MODEL slx_e30d3c3d6ad5
CONFIG AbsTol = auto
CONFIG FixedStep = 0.001
CONFIG MaxStep = auto
CONFIG MinStep = auto
CONFIG RelTol = 1e-3
CONFIG SampleTimeConstraint = Unconstrained
CONFIG Solver = ode4
CONFIG SolverMode = Auto
CONFIG SolverName = ode4
CONFIG StartTime = 0.0
CONFIG StopTime = 15
BLOCK [SubSystem] Control Law Block
  Ports = [2, 1]
  RequestExecContextInheritance = off
BLOCK [Constant] Control Law Block/Constant
  Value = d
BLOCK [SubSystem] Control Law Block/MATLAB Function
  ErrorFcn = Stateflow.Translate.translate
  PermitHierarchicalResolution = ExplicitOnly
  Ports = [2, 1]
  RequestExecContextInheritance = off
  SFBlockType = MATLAB Function
  TreatAsAtomicUnit = on
BLOCK [Demux] Control Law Block/MATLAB Function/ Demux 
  Outputs = 1
  Ports = [1, 1]
BLOCK [S-Function] Control Law Block/MATLAB Function/ SFunction 
  EnableBusSupport = on
  FunctionName = sf_sfun
  PortCounts = [2 2]
  Ports = [2, 2]
  Tag = Stateflow S-Function StaticControl 2
BLOCK [Terminator] Control Law Block/MATLAB Function/ Terminator 
BLOCK [Outport] Control Law Block/MATLAB Function/K_inv
  IconDisplay = Port number
BLOCK [Inport] Control Law Block/MATLAB Function/d
  IconDisplay = Port number
BLOCK [Inport] Control Law Block/MATLAB Function/theta
  IconDisplay = Port number
  Port = 2
BLOCK [Product] Control Law Block/Product
  InputSameDT = off
  Multiplication = Matrix(*)
  OutDataTypeStr = Inherit: Inherit via internal rule
  Ports = [2, 1]
  RndMeth = Floor
  SaturateOnIntegerOverflow = off
BLOCK [Inport] Control Law Block/W
  IconDisplay = Port number
BLOCK [Inport] Control Law Block/theta
  IconDisplay = Port number
  Port = 2
BLOCK [Outport] Control Law Block/u_m
  IconDisplay = Port number
BLOCK [SubSystem] DKM
  Ports = [1, 3]
  RequestExecContextInheritance = off
BLOCK [Demux] DKM/Demux
  DisplayOption = bar
  Outputs = 2
  Ports = [1, 2]
BLOCK [Constant] DKM/F_inv
  Value = [r/2 r/2; r/(2*L) -r/(2*L)]
BLOCK [Fcn] DKM/Fcn
  Expr = cos(u)
BLOCK [Fcn] DKM/Fcn1
  Expr = sin(u)
BLOCK [Integrator] DKM/Integrator
  InitialCondition = theta0
  Ports = [1, 1]
BLOCK [Product] DKM/Product
  InputSameDT = off
  OutDataTypeStr = Inherit: Inherit via internal rule
  Ports = [2, 1]
  RndMeth = Floor
  SaturateOnIntegerOverflow = off
BLOCK [Product] DKM/Product1
  InputSameDT = off
  OutDataTypeStr = Inherit: Inherit via internal rule
  Ports = [2, 1]
  RndMeth = Floor
  SaturateOnIntegerOverflow = off
BLOCK [Scope] DKM/Scope
  Floating = off
  NumInputPorts = 1
  Ports = [1]
BLOCK [ToWorkspace] DKM/To Workspace
  FixptAsFi = on
  MaxDataPoints = inf
  Ports = [1]
  SampleTime = -1
  Save2DSignal = 3-D array (concatenate along third dimension)
  VariableName = u
BLOCK [Inport] DKM/qm_dot
  IconDisplay = Port number
BLOCK [Outport] DKM/theta
  IconDisplay = Port number
  Port = 3
BLOCK [Product] DKM/u_m Func
  InputSameDT = off
  Multiplication = Matrix(*)
  OutDataTypeStr = Inherit: Inherit via internal rule
  Ports = [2, 1]
  RndMeth = Floor
  SaturateOnIntegerOverflow = off
BLOCK [Outport] DKM/x_dot
  IconDisplay = Port number
BLOCK [Outport] DKM/y_dot
  IconDisplay = Port number
  Port = 2
BLOCK [Gain] Gain
  Gain = K
  OutDataTypeStr = Inherit: Inherit via internal rule
  ParamDataTypeStr = Inherit: Inherit via internal rule
  SaturateOnIntegerOverflow = off
BLOCK [Gain] IKM
  Gain = [1/r_e L_e/r_e; 1/r_e  -L_e/r_e]
  Multiplication = Matrix(K*u) (u vector)
  OutDataTypeStr = Inherit: Inherit via internal rule
  ParamDataTypeStr = Inherit: Inherit via internal rule
  SaturateOnIntegerOverflow = off
BLOCK [SubSystem] Localization
  Ports = [3, 3]
  RequestExecContextInheritance = off
BLOCK [Integrator] Localization/Integrator1
  InitialCondition = x0
  Ports = [1, 1]
BLOCK [Integrator] Localization/Integrator2
  InitialCondition = y0
  Ports = [1, 1]
BLOCK [Mux] Localization/Mux
  DisplayOption = bar
  Inputs = 2
  Ports = [2, 1]
BLOCK [Mux] Localization/Mux1
  DisplayOption = bar
  Inputs = 2
  Ports = [2, 1]
BLOCK [Fcn] Localization/hx Func
  Expr = u(1)+d*cos(u(2))
BLOCK [Fcn] Localization/hy Func
  Expr = u(1)+d*sin(u(2))
BLOCK [Outport] Localization/theta
  IconDisplay = Port number
  Port = 3
BLOCK [Inport] Localization/theta 
  IconDisplay = Port number
  Port = 3
BLOCK [Outport] Localization/x
  IconDisplay = Port number
BLOCK [Inport] Localization/x_dot
  IconDisplay = Port number
BLOCK [Outport] Localization/y
  IconDisplay = Port number
  Port = 2
BLOCK [Inport] Localization/y_dot
  IconDisplay = Port number
  Port = 2
BLOCK [Mux] Mux
  DisplayOption = bar
  Inputs = 2
  Ports = [2, 1]
BLOCK [Mux] Mux1
  DisplayOption = bar
  Inputs = 2
  Ports = [2, 1]
BLOCK [Mux] Mux2
  DisplayOption = bar
  Inputs = 2
  Ports = [2, 1]
BLOCK [Mux] Mux3
  DisplayOption = bar
  Inputs = 3
  Ports = [3, 1]
BLOCK [Sum] Sum
  IconShape = round
  InputSameDT = off
  Inputs = -+|
  OutDataTypeStr = Inherit: Inherit via internal rule
  Ports = [2, 1]
  SaturateOnIntegerOverflow = off
BLOCK [Sum] Sum1
  IconShape = round
  InputSameDT = off
  Inputs = |++
  OutDataTypeStr = Inherit: Inherit via internal rule
  Ports = [2, 1]
  SaturateOnIntegerOverflow = off
BLOCK [ToWorkspace] To Workspace
  FixptAsFi = on
  MaxDataPoints = inf
  Ports = [1]
  SampleTime = -1
  Save2DSignal = 3-D array (concatenate along third dimension)
  VariableName = hd
BLOCK [ToWorkspace] To Workspace1
  FixptAsFi = on
  MaxDataPoints = inf
  Ports = [1]
  SampleTime = -1
  Save2DSignal = 3-D array (concatenate along third dimension)
  VariableName = h
BLOCK [ToWorkspace] To Workspace2
  FixptAsFi = on
  MaxDataPoints = inf
  Ports = [1]
  SampleTime = -1
  Save2DSignal = 3-D array (concatenate along third dimension)
  VariableName = error
BLOCK [SubSystem] Trajectory Generator
  Ports = [0, 4]
  RequestExecContextInheritance = off
BLOCK [SubSystem] Trajectory Generator/Circular Trajectory
  Ports = [0, 1]
  RequestExecContextInheritance = off
BLOCK [Constant] Trajectory Generator/Circular Trajectory/Constant
  Value = wd
BLOCK [Constant] Trajectory Generator/Circular Trajectory/Constant1
  Value = R
BLOCK [Fcn] Trajectory Generator/Circular Trajectory/Fcn
  Expr = u+pi/2
BLOCK [Integrator] Trajectory Generator/Circular Trajectory/Integrator
  Ports = [1, 1]
BLOCK [Mux] Trajectory Generator/Circular Trajectory/Mux
  DisplayOption = bar
  Inputs = 3
  Ports = [3, 1]
BLOCK [Mux] Trajectory Generator/Circular Trajectory/Mux1
  DisplayOption = bar
  Ports = [4, 1]
BLOCK [ToWorkspace] Trajectory Generator/Circular Trajectory/To Workspace
  FixptAsFi = on
  MaxDataPoints = inf
  Ports = [1]
  SampleTime = -1
  Save2DSignal = 3-D array (concatenate along third dimension)
  VariableName = thetad
BLOCK [Outport] Trajectory Generator/Circular Trajectory/[hd; hd_dot]
  IconDisplay = Port number
BLOCK [Fcn] Trajectory Generator/Circular Trajectory/xd Func
  Expr = u(3)*cos(u(2))
BLOCK [Fcn] Trajectory Generator/Circular Trajectory/xd_dot Func
  Expr = -u(3)*u(1)*sin(u(2))
BLOCK [Fcn] Trajectory Generator/Circular Trajectory/yd Func
  Expr = u(3)*sin(u(2))
BLOCK [Fcn] Trajectory Generator/Circular Trajectory/yd_dot Func
  Expr = u(3)*u(1)*cos(u(2))
BLOCK [Constant] Trajectory Generator/Constant
  Value = mode
BLOCK [Demux] Trajectory Generator/Demux
  DisplayOption = bar
  Ports = [1, 4]
BLOCK [SubSystem] Trajectory Generator/Fixed Point Tracking
  Ports = [0, 1]
  RequestExecContextInheritance = off
BLOCK [Constant] Trajectory Generator/Fixed Point Tracking/Constant
  Value = D_fixed
BLOCK [Constant] Trajectory Generator/Fixed Point Tracking/Constant1
  Value = 0
BLOCK [Mux] Trajectory Generator/Fixed Point Tracking/Mux
  DisplayOption = bar
  Inputs = 3
  Ports = [3, 1]
BLOCK [Outport] Trajectory Generator/Fixed Point Tracking/[hd; 0 0]
  IconDisplay = Port number
BLOCK [Switch] Trajectory Generator/Switch
  Criteria = u2 > Threshold
  InputSameDT = off
  SaturateOnIntegerOverflow = off
BLOCK [Outport] Trajectory Generator/xd
  IconDisplay = Port number
BLOCK [Outport] Trajectory Generator/xd_dot
  IconDisplay = Port number
  Port = 3
BLOCK [Outport] Trajectory Generator/yd
  IconDisplay = Port number
  Port = 2
BLOCK [Outport] Trajectory Generator/yd_dot
  IconDisplay = Port number
  Port = 4
LINE Control Law Block/Constant:1 -> Control Law Block/MATLAB Function:1
LINE Control Law Block/MATLAB Function:1 -> Control Law Block/Product:1
LINE Control Law Block/Product:1 -> Control Law Block/u_m:1
LINE Control Law Block/W:1 -> Control Law Block/Product:2
LINE Control Law Block/theta:1 -> Control Law Block/MATLAB Function:2
LINE Control Law Block:1 -> IKM:1
LINE DKM/Demux:1 -> DKM/Product1:1
LINE DKM/Demux:1 -> DKM/Product:1
LINE DKM/Demux:2 -> DKM/Integrator:1
LINE DKM/F_inv:1 -> DKM/u_m Func:1
LINE DKM/Fcn1:1 -> DKM/Product1:2
LINE DKM/Fcn:1 -> DKM/Product:2
LINE DKM/Integrator:1 -> DKM/Fcn1:1
LINE DKM/Integrator:1 -> DKM/Fcn:1
LINE DKM/Integrator:1 -> DKM/theta:1
LINE DKM/Product1:1 -> DKM/y_dot:1
LINE DKM/Product:1 -> DKM/x_dot:1
LINE DKM/qm_dot:1 -> DKM/u_m Func:2
LINE DKM/u_m Func:1 -> DKM/Demux:1
LINE DKM/u_m Func:1 -> DKM/Scope:1
LINE DKM/u_m Func:1 -> DKM/To Workspace:1
LINE DKM:1 -> Localization:1
LINE DKM:2 -> Localization:2
LINE DKM:3 -> Localization:3
LINE Gain:1 -> Sum1:1
LINE IKM:1 -> DKM:1
LINE Localization/Integrator1:1 -> Localization/Mux:1
LINE Localization/Integrator2:1 -> Localization/Mux1:1
LINE Localization/Mux1:1 -> Localization/hy Func:1
LINE Localization/Mux:1 -> Localization/hx Func:1
LINE Localization/hx Func:1 -> Localization/x:1
LINE Localization/hy Func:1 -> Localization/y:1
LINE Localization/theta :1 -> Localization/Mux1:2
LINE Localization/theta :1 -> Localization/Mux:2
LINE Localization/theta :1 -> Localization/theta:1
LINE Localization/x_dot:1 -> Localization/Integrator1:1
LINE Localization/y_dot:1 -> Localization/Integrator2:1
LINE Localization:1 -> Mux2:1
LINE Localization:1 -> Mux3:1
LINE Localization:2 -> Mux2:2
LINE Localization:2 -> Mux3:2
LINE Localization:3 -> Control Law Block:2
LINE Localization:3 -> Mux3:3
LINE Mux1:1 -> Sum1:2
LINE Mux2:1 -> Sum:1
LINE Mux3:1 -> To Workspace1:1
LINE Mux:1 -> Sum:2
LINE Mux:1 -> To Workspace:1
LINE Sum1:1 -> Control Law Block:1
LINE Sum:1 -> Gain:1
LINE Sum:1 -> To Workspace2:1
LINE Trajectory Generator/Circular Trajectory/Constant1:1 -> Trajectory Generator/Circular Trajectory/Mux:3
LINE Trajectory Generator/Circular Trajectory/Constant:1 -> Trajectory Generator/Circular Trajectory/Integrator:1
LINE Trajectory Generator/Circular Trajectory/Constant:1 -> Trajectory Generator/Circular Trajectory/Mux:1
LINE Trajectory Generator/Circular Trajectory/Fcn:1 -> Trajectory Generator/Circular Trajectory/To Workspace:1
LINE Trajectory Generator/Circular Trajectory/Integrator:1 -> Trajectory Generator/Circular Trajectory/Fcn:1
LINE Trajectory Generator/Circular Trajectory/Integrator:1 -> Trajectory Generator/Circular Trajectory/Mux:2
LINE Trajectory Generator/Circular Trajectory/Mux1:1 -> Trajectory Generator/Circular Trajectory/[hd; hd_dot]:1
LINE Trajectory Generator/Circular Trajectory/Mux:1 -> Trajectory Generator/Circular Trajectory/xd Func:1
LINE Trajectory Generator/Circular Trajectory/Mux:1 -> Trajectory Generator/Circular Trajectory/xd_dot Func:1
LINE Trajectory Generator/Circular Trajectory/Mux:1 -> Trajectory Generator/Circular Trajectory/yd Func:1
LINE Trajectory Generator/Circular Trajectory/Mux:1 -> Trajectory Generator/Circular Trajectory/yd_dot Func:1
LINE Trajectory Generator/Circular Trajectory/xd Func:1 -> Trajectory Generator/Circular Trajectory/Mux1:1
LINE Trajectory Generator/Circular Trajectory/xd_dot Func:1 -> Trajectory Generator/Circular Trajectory/Mux1:3
LINE Trajectory Generator/Circular Trajectory/yd Func:1 -> Trajectory Generator/Circular Trajectory/Mux1:2
LINE Trajectory Generator/Circular Trajectory/yd_dot Func:1 -> Trajectory Generator/Circular Trajectory/Mux1:4
LINE Trajectory Generator/Circular Trajectory:1 -> Trajectory Generator/Switch:3
LINE Trajectory Generator/Constant:1 -> Trajectory Generator/Switch:2
LINE Trajectory Generator/Demux:1 -> Trajectory Generator/xd:1
LINE Trajectory Generator/Demux:2 -> Trajectory Generator/yd:1
LINE Trajectory Generator/Demux:3 -> Trajectory Generator/xd_dot:1
LINE Trajectory Generator/Demux:4 -> Trajectory Generator/yd_dot:1
LINE Trajectory Generator/Fixed Point Tracking/Constant1:1 -> Trajectory Generator/Fixed Point Tracking/Mux:2
LINE Trajectory Generator/Fixed Point Tracking/Constant1:1 -> Trajectory Generator/Fixed Point Tracking/Mux:3
LINE Trajectory Generator/Fixed Point Tracking/Constant:1 -> Trajectory Generator/Fixed Point Tracking/Mux:1
LINE Trajectory Generator/Fixed Point Tracking/Mux:1 -> Trajectory Generator/Fixed Point Tracking/[hd; 0 0]:1
LINE Trajectory Generator/Fixed Point Tracking:1 -> Trajectory Generator/Switch:1
LINE Trajectory Generator/Switch:1 -> Trajectory Generator/Demux:1
LINE Trajectory Generator:1 -> Mux:1
LINE Trajectory Generator:2 -> Mux:2
LINE Trajectory Generator:3 -> Mux1:1
LINE Trajectory Generator:4 -> Mux1:2
CHART Control Law Block/MATLAB Function states=1 transitions=1
  STATE_LABEL 'eML_blk_kernel()'
  STATE_LABEL 'SCRIPT:\nfunction K_inv = Find_K_Inv(d,theta)\n\nK_inv = inv([cos(theta) -d*sin(theta); sin(theta) d*cos(theta)]);\nend'
